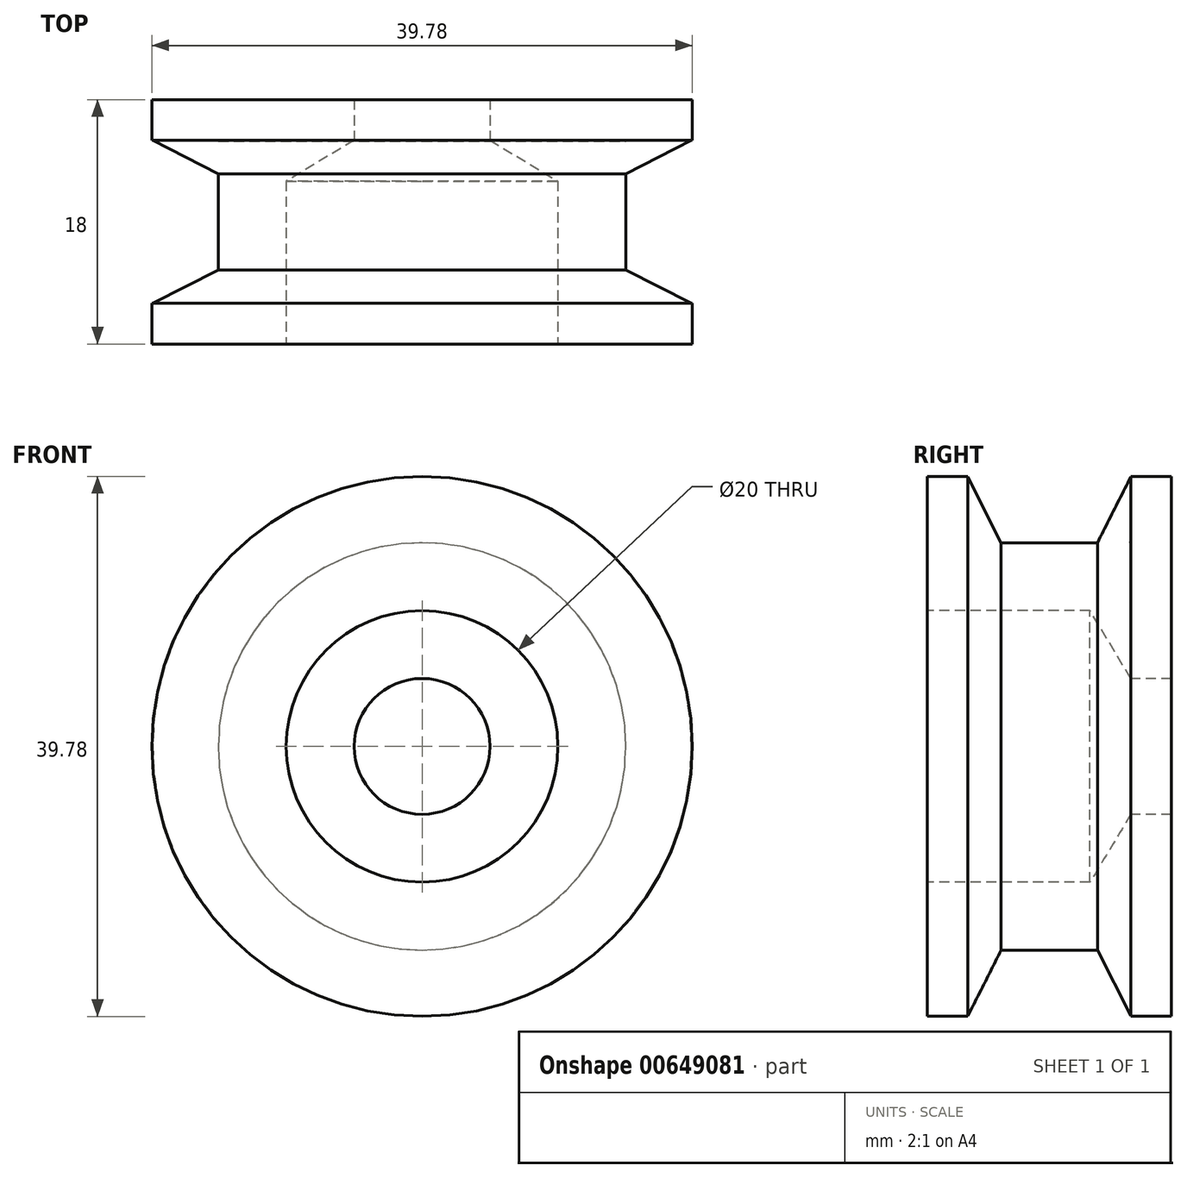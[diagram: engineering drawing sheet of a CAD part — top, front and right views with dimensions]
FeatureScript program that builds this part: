
annotation { "Feature Type Name" : "Feature", "Feature Type Description" : "" }
export const myFeature = defineFeature(function(context is Context, id is Id, definition is map)
    precondition{}
    {
        {
            var Q0;
            Q0=qCreatedBy(makeId("Front.planeOp"),FACE);
            var sketch = newSketch(context, id + "F0", { "sketchPlane" : qUnion([Q0])});
            skCircle(sketch, "E0", {"center": v(0, 0) * mm, "radius": 15 * mm});
            skCircle(sketch, "E1", {"center": v(0, 0) * mm, "radius": 20.05 * mm});
            skCircle(sketch, "E2", {"center": v(0, 0) * mm, "radius": 9.9 * mm});
            skCircle(sketch, "E3", {"center": v(0, 0) * mm, "radius": 5.07 * mm});
            skSolve(sketch);
        }
        {
            var Q0;
            Q0=makeQuery(id+"F0.imprint","IMPRINT",FACE,{"disambiguationData":[TD([[makeQuery(id+"F0.imprint","IMPRINT",EDGE,{"derivedFrom":sQuery(id+"F0.wireOp",EDGE,"E0")}),1.0]])]});
            var Q1;
            Q1=makeQuery(id+"F0.imprint","IMPRINT",FACE,{"disambiguationData":[TD([[makeQuery(id+"F0.imprint","IMPRINT",EDGE,{"derivedFrom":sQuery(id+"F0.wireOp",EDGE,"E3")}),1.0]])]});
            var Q2;
            Q2=makeQuery(id+"F0.imprint","IMPRINT",FACE,{"disambiguationData":[TD([[makeQuery(id+"F0.imprint","IMPRINT",EDGE,{"derivedFrom":sQuery(id+"F0.wireOp",EDGE,"E2")}),1.0]])]});
            extrude(context, id + "F1", {"entities" : qUnion([Q0, Q1, Q2]), "endBound" : BoundingType.SYMMETRIC, "depth" : 18 * mm, "offsetDistance" : 25 * mm});
        }
        {
            var Q0;
            Q0=makeQuery(id+"F1.opExtrude","CAP_FACE",FACE,{"disambiguationData":[OSD([sQuery(id+"F0.wireOp",EDGE,"E0")])],"isStart":false});
            var sketch = newSketch(context, id + "F2", { "sketchPlane" : qUnion([Q0])});
            skCircle(sketch, "E4", {"center": v(0, 0) * mm, "radius": 19.89 * mm});
            skSolve(sketch);
        }
        {
            var Q0;
            Q0=makeQuery(id+"F2.imprint","IMPRINT",FACE,{"disambiguationData":[TD([[makeQuery(id+"F2.imprint","IMPRINT",EDGE,{"derivedFrom":sQuery(id+"F2.wireOp",EDGE,"E4")}),1.0]])]});
            extrude(context, id + "F3", {"entities" : qUnion([Q0]), "oppositeDirection" : true, "depth" : 3 * mm, "offsetDistance" : 25 * mm});
        }
        {
            var Q0;
            Q0=makeQuery(id+"F3.opExtrude","SWEPT_BODY",BODY,{"disambiguationData":[OSD([sQuery(id+"F0.wireOp",EDGE,"E0"),sQuery(id+"F2.wireOp",EDGE,"E4")])]});
            var Q1;
            Q1=qCreatedBy(makeId("Front.planeOp"),FACE);
            mirror(context, id + "F4", {"operationType" : NewBodyOperationType.ADD, "entities" : qUnion([Q0]), "mirrorPlane" : qUnion([Q1])});
        }
        {
            var Q0;
            Q0=qCreatedBy(makeId("Right.planeOp"),FACE);
            var sketch = newSketch(context, id + "F5", { "sketchPlane" : qUnion([Q0])});
            skLineSegment(sketch, "E5", {"start": v(-6, 19.84) * mm, "end": v(-3.5, 14.92) * mm});
            skLineSegment(sketch, "E6.MirrorCS", {"start": v(6, 19.84) * mm, "end": v(3.5, 14.92) * mm});
            skLineSegment(sketch, "E7", {"start": v(3.5, 14.92) * mm, "end": v(5.95, 14.92) * mm});
            skLineSegment(sketch, "E8", {"start": v(5.95, 14.92) * mm, "end": v(6, 19.84) * mm});
            skLineSegment(sketch, "E9", {"start": v(-6, 19.84) * mm, "end": v(-6, 14.92) * mm});
            skLineSegment(sketch, "E10", {"start": v(-6, 14.92) * mm, "end": v(-3.5, 14.92) * mm});
            skSolve(sketch);
        }
        {
            var Q0;
            Q0=makeQuery(id+"F5.imprint","IMPRINT",FACE,{"disambiguationData":[TD([[makeQuery(id+"F5.imprint","IMPRINT",EDGE,{"derivedFrom":sQuery(id+"F5.wireOp",EDGE,"E5")}),-1.0]])]});
            var Q1;
            Q1=makeQuery(id+"F5.imprint","IMPRINT",FACE,{"disambiguationData":[TD([[makeQuery(id+"F5.imprint","IMPRINT",EDGE,{"derivedFrom":sQuery(id+"F5.wireOp",EDGE,"E6.MirrorCS")}),1.0]])]});
            var Q2;
            Q2=makeQuery(id+"F1.opExtrude","SWEPT_FACE",FACE,{"disambiguationData":[OSD([sQuery(id+"F0.wireOp",EDGE,"E0")])]});
            revolve(context, id + "F6", {"operationType" : NewBodyOperationType.ADD, "entities" : qUnion([Q0, Q1]), "axis" : qUnion([Q2]), "revolveType" : RevolveType.FULL});
        }
        {
            var Q0;
            Q0=sQuery(id+"F2.wireOp",VERTEX,"E4.center");
            var Q1;
            Q1=makeQuery(id+"F1.opExtrude","SWEPT_BODY",BODY,{"disambiguationData":[OSD([sQuery(id+"F0.wireOp",EDGE,"E0")])]});
            hole(context, id + "F7", {"style" : HoleStyle.SIMPLE, "endStyle" : HoleEndStyle.THROUGH, "holeDiameter" : 10 * mm, "majorDiameter" : 5 * mm, "isTappedThrough" : true, "tappedDepth" : 12 * mm, "tapClearance" : 3, "startFromSketch" : true, "locations" : qUnion([Q0]), "scope" : qUnion([Q1])});
        }
        {
            var Q0;
            Q0=sQuery(id+"F2.wireOp",VERTEX,"E4.center");
            var Q1;
            Q1=makeQuery(id+"F1.opExtrude","SWEPT_BODY",BODY,{"disambiguationData":[OSD([sQuery(id+"F0.wireOp",EDGE,"E0")])]});
            hole(context, id + "F8", {"style" : HoleStyle.SIMPLE, "endStyle" : HoleEndStyle.BLIND, "holeDiameter" : 20 * mm, "majorDiameter" : 5 * mm, "holeDepth" : 12 * mm, "isTappedThrough" : true, "tappedDepth" : 12 * mm, "tapClearance" : 3, "startFromSketch" : true, "locations" : qUnion([Q0]), "scope" : qUnion([Q1])});
        }
    });
